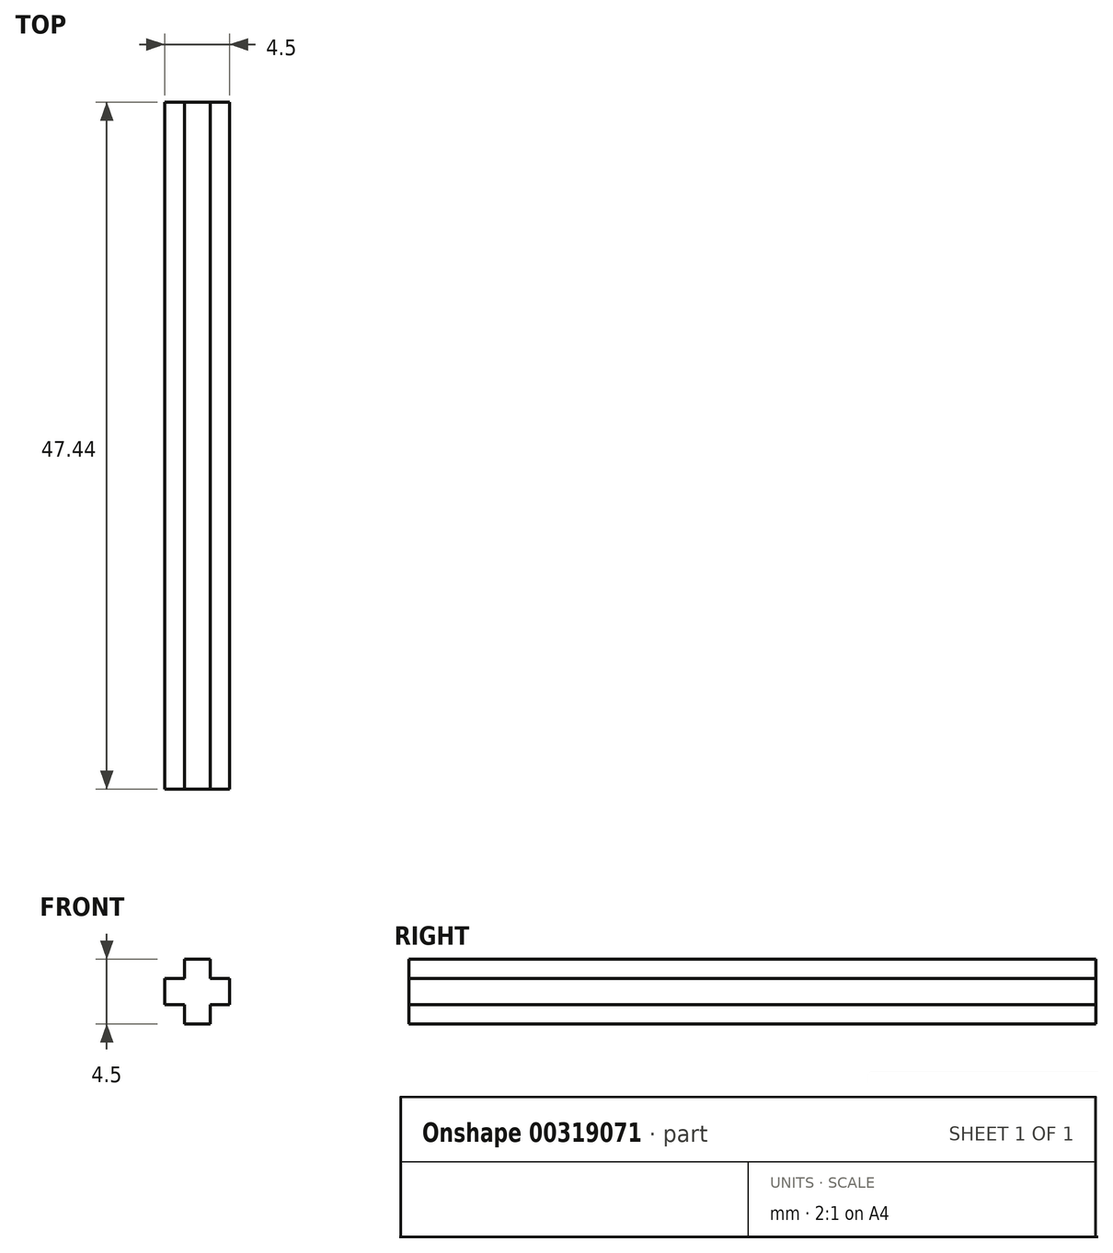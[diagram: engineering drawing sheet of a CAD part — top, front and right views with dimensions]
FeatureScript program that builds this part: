
annotation { "Feature Type Name" : "Feature", "Feature Type Description" : "" }
export const myFeature = defineFeature(function(context is Context, id is Id, definition is map)
    precondition{}
    {
        {
            var Q0;
            Q0=qCreatedBy(makeId("Front.planeOp"),FACE);
            var sketch = newSketch(context, id + "F0", { "sketchPlane" : qUnion([Q0])});
            skLineSegment(sketch, "E0.bottom", {"start": v(-2.25, 0.89) * mm, "end": v(2.25, 0.89) * mm});
            skLineSegment(sketch, "E0.top", {"start": v(-2.25, -0.89) * mm, "end": v(2.25, -0.89) * mm});
            skLineSegment(sketch, "E0.left", {"start": v(-2.25, 0.9) * mm, "end": v(-2.25, -0.89) * mm});
            skLineSegment(sketch, "E0.right", {"start": v(2.25, 0.9) * mm, "end": v(2.25, -0.89) * mm});
            skLineSegment(sketch, "E1.bottom", {"start": v(-0.9, 2.25) * mm, "end": v(0.9, 2.25) * mm});
            skLineSegment(sketch, "E1.top", {"start": v(-0.9, -2.25) * mm, "end": v(0.9, -2.25) * mm});
            skLineSegment(sketch, "E1.left", {"start": v(-0.89, 2.25) * mm, "end": v(-0.9, -2.25) * mm});
            skLineSegment(sketch, "E1.right", {"start": v(0.89, 2.25) * mm, "end": v(0.89, -2.25) * mm});
            skLineSegment(sketch, "E2", {"start": v(0, -0.9) * mm, "end": v(0, 0.9) * mm});
            skLineSegment(sketch, "E3", {"start": v(-0.9, 0) * mm, "end": v(0.9, 0) * mm});
            skPoint(sketch, "E4", {"position": v(0, 0) * mm});
            skSolve(sketch);
        }
        {
            var Q0;
            Q0 = qSketchRegion(id + "F0", true);
            extrude(context, id + "F1", {"entities" : qUnion([Q0]), "endBound" : BoundingType.SYMMETRIC, "depth" : 47.44 * mm});
        }
    });
